# Revit family: Enchufe cerrado 380_415V
name_source: partatom
category: Installations électriques
revit_build: Autodesk Revit 2018 (Build: 20170223_1515(x64)
units: mm (PartAtom-declared; Revit-internal decimal feet)

## family parameters
Conserver l'orientation des annotations = Non
Cote de connecteur circulaire = Utiliser le diamètre
Couper avec des vides une fois chargée = Non
Hôte = Face
Partagée = Non
Point de calcul de pièce = Non
Type d'élément = Normal

## types (4) — shared parameters
Elévation par défaut = 1000 mm  [stored 3.28084 ft]
Estándar CEI o NFC = CEI
Fabricant = Legrand
Familia produce = 0852-P17
Temperatura maxima de uso = +40
Temperatura minima de uso = -25
Tension V = 400 V  50/60 Hz rojo
Toma estándar internacional para montaje empotrado o montaje en superficie con accesorio permite la conexión de dispositivos de alimentación = Toma estándar internacional para montaje empotrado o montaje en superficie con accesorio permite la conexión de dispositivos de alimentación
altura mm = 105 mm  [stored 0.344488 ft]
ancho mm = 125 mm  [stored 0.410105 ft]
color característico = rojo
distancia de fijación horizontal mm = 91 mm
distancia de fijación vertical mm = 87 mm
intensidad A = 16 A
materia de la caja = plástico
posición de la tierra h = 6
profundidad de empotrar mm = 81 mm  [stored 0.265748 ft]
profundidad mm = 120 mm  [stored 0.393701 ft]
sin halogeno = Oui
tipo de conexión = conexión por tonillo
tipo de enclavamiento = enclavamiento eléctrico y mecánico

## per-type parameters (varying)
| type | Description | Modèle | clase de protección IP | numero de polos | resistencia a los choques IK |
| P17 - IP55 - 380/415V-16A -3P+N+T | LG-0357322 Enchufe cerrado P17 - IP55 - 380/415V - 16A -3P+T | LG-057322 | IP55 | 5 | 13 |
| P17 - IP55 - 380/415V - 16A -3P+T | LG-0357321 Enchufe cerrado P17 - IP55 - 380/415V - 16A -3P+T | LG-057321 | IP55 | 4 | 12 |
| P17 - IP44 - 380/415V-16A -3P+N+T | LG-0357302 Enchufe cerrado P17 - IP44 - 380/415V - 16A -3P+N+T | LG-057302 | IP44 | 5 | 10 |
| P17 - IP44 - 380/415V - 16A -3P+T | LG-0357301 Enchufe cerrado P17 - IP44 - 380/415V - 16A -3P+T | LG-057301 | IP44 | 4 | 09 |

note: [stored X ft] marks values corroborated as IEEE doubles in the binary element streams (Revit-internal decimal feet)
